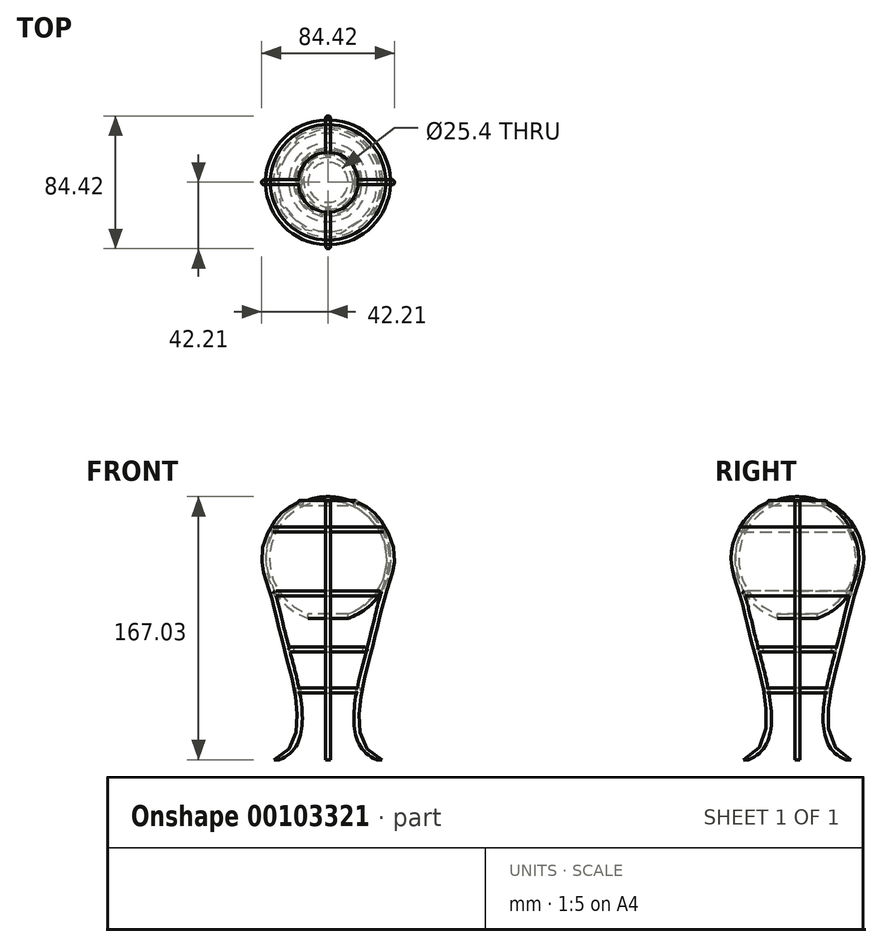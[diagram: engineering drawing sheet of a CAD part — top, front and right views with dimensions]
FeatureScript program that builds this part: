
annotation { "Feature Type Name" : "Feature", "Feature Type Description" : "" }
export const myFeature = defineFeature(function(context is Context, id is Id, definition is map)
    precondition{}
    {
        {
            var Q0;
            Q0=qCreatedBy(makeId("Front.planeOp"),FACE);
            var sketch = newSketch(context, id + "F0", { "sketchPlane" : qUnion([Q0])});
            skArc(sketch, "E0", {"start": v(0, 39.68) * mm, "mid": v(-39.68, 0) * mm, "end": v(0, -39.68) * mm});
            skLineSegment(sketch, "E1", {"start": v(0, -55.2) * mm, "end": v(0, 54.64) * mm});
            skSolve(sketch);
        }
        {
            var Q0;
            {var subQ0=sQuery(id+"F0.wireOp",EDGE,"E0");Q0=makeQuery(id+"F0.imprint","IMPRINT",FACE,{"disambiguationData":[TD([[makeQuery(id+"F0.imprint","IMPRINT",EDGE,{"derivedFrom":subQ0}),1.0]])]});}
            var Q1;
            Q1=sQuery(id+"F0.wireOp",EDGE,"E1");
            revolve(context, id + "F1", {"entities" : qUnion([Q0]), "axis" : qUnion([Q1]), "revolveType" : RevolveType.FULL});
        }
        {
            var Q0;
            Q0=qCreatedBy(makeId("Top.planeOp"),FACE);
            var sketch = newSketch(context, id + "F2", { "sketchPlane" : qUnion([Q0])});
            skCircle(sketch, "E2", {"center": v(0, 0) * mm, "radius": 12.7 * mm});
            skSolve(sketch);
        }
        {
            var Q0;
            Q0 = qSketchRegion(id + "F2", true);
            extrude(context, id + "F3", {"entities" : qUnion([Q0]), "operationType" : NewBodyOperationType.ADD, "oppositeDirection" : true, "depth" : 127 * mm});
        }
        {
            var Q0;
            Q0=makeQuery(id+"F3.opExtrude","SWEPT_FACE",FACE,{"disambiguationData":[OSD([sQuery(id+"F2.wireOp",EDGE,"E2")])]});
            var Q1;
            Q1=makeQuery(id+"F3.opExtrude","CAP_FACE",FACE,{"disambiguationData":[OSD([sQuery(id+"F2.wireOp",EDGE,"E2")])],"isStart":false});
            var Q2;
            Q2=makeQuery(id+"F1.opRevolve","SWEPT_BODY",BODY,{"disambiguationData":[OSD([sQuery(id+"F0.wireOp",EDGE,"E0"),sQuery(id+"F0.wireOp",EDGE,"E1")])]});
            shell(context, id + "F4", {"entities" : qUnion([Q0, Q1]), "parts" : qUnion([Q2]), "thickness" : 2.54 * mm});
        }
        {
            var Q0;
            Q0=qCreatedBy(makeId("Right.planeOp"),FACE);
            var sketch = newSketch(context, id + "F5", { "sketchPlane" : qUnion([Q0])});
            skCircle(sketch, "E3", {"center": v(-35.08, 18.94) * mm, "radius": 1.59 * mm});
            skCircle(sketch, "E4", {"center": v(-33.1, -21.72) * mm, "radius": 1.59 * mm});
            skCircle(sketch, "E5", {"center": v(-17.43, 35.83) * mm, "radius": 1.59 * mm});
            skSolve(sketch);
        }
        {
            var Q0;
            Q0=qCreatedBy(makeId("Front.planeOp"),FACE);
            var sketch = newSketch(context, id + "F6", { "sketchPlane" : qUnion([Q0])});
            skLineSegment(sketch, "E6", {"start": v(0, 56.6) * mm, "end": v(0, -57.7) * mm});
            skSolve(sketch);
        }
        {
            var Q0;
            Q0=qCreatedBy(makeId("Top.planeOp"),FACE);
            cPlane(context, id + "F7", {"entities" : qUnion([Q0]), "cplaneType" : CPlaneType.OFFSET, "offset" : 36.07 * mm, "width" : 152.4 * mm, "height" : 152.4 * mm});
        }
        {
            var Q0;
            Q0 = qSketchRegion(id + "F5", true);
            var Q1;
            Q1=sQuery(id+"F6.wireOp",EDGE,"E6");
            revolve(context, id + "F8", {"entities" : qUnion([Q0]), "axis" : qUnion([Q1]), "revolveType" : RevolveType.FULL});
        }
        {
            var Q0;
            Q0=qCreatedBy(id+"F7.planeOp",FACE);
            var sketch = newSketch(context, id + "F9", { "sketchPlane" : qUnion([Q0])});
            skCircle(sketch, "E7", {"center": v(-17.61, 0) * mm, "radius": 1.59 * mm});
            skSolve(sketch);
        }
        {
            var Q0;
            Q0=qCreatedBy(makeId("Front.planeOp"),FACE);
            var sketch = newSketch(context, id + "F10", { "sketchPlane" : qUnion([Q0])});
            skFitSpline(sketch, "E8", {"points": [v(-18.71, 36.13) * mm, v(-36.5, 19.47) * mm, v(-41.87, 0) * mm, v(-36.3, -22.17) * mm, v(-27.15, -58.35) * mm, v(-33.84, -127.35) * mm], "startDerivative": vector(-158.7, -63.01) * mm, "endDerivative": vector(-246.66, -91.65) * mm});
            skSolve(sketch);
        }
        {
            var Q0;
            Q0 = qSketchRegion(id + "F9", true);
            var Q1;
            Q1 = qConstructionFilter(qBodyType(qCreatedBy(id + "F10" ,EDGE), BodyType.WIRE), ConstructionObject.NO);
            sweep(context, id + "F11", {"profiles" : qUnion([Q0]), "path" : qUnion([Q1]), "keepProfileOrientation" : true});
        }
        {
            var Q0;
            Q0=makeQuery(id+"F11.opSweep","SWEPT_BODY",BODY,{"disambiguationData":[OSD([sQuery(id+"F9.wireOp",EDGE,"E7"),sQuery(id+"F10.wireOp",EDGE,"E8")])]});
            var Q1;
            Q1=sQuery(id+"F6.wireOp",EDGE,"E6");
            transform(context, id + "F12", {"entities" : qUnion([Q0]), "transformType" : TransformType.ROTATION, "transformAxis" : qUnion([Q1]), "angle" : 90 * degree, "makeCopy" : true});
        }
        {
            var Q0;
            Q0=makeQuery(id+"F11.opSweep","SWEPT_BODY",BODY,{"disambiguationData":[OSD([sQuery(id+"F9.wireOp",EDGE,"E7"),sQuery(id+"F10.wireOp",EDGE,"E8")])]});
            var Q1;
            Q1=sQuery(id+"F6.wireOp",EDGE,"E6");
            transform(context, id + "F13", {"entities" : qUnion([Q0]), "transformType" : TransformType.ROTATION, "transformAxis" : qUnion([Q1]), "angle" : 180 * degree, "makeCopy" : true});
        }
        {
            var Q0;
            Q0=makeQuery(id+"F11.opSweep","SWEPT_BODY",BODY,{"disambiguationData":[OSD([sQuery(id+"F9.wireOp",EDGE,"E7"),sQuery(id+"F10.wireOp",EDGE,"E8")])]});
            var Q1;
            Q1=sQuery(id+"F6.wireOp",EDGE,"E6");
            transform(context, id + "F14", {"entities" : qUnion([Q0]), "transformType" : TransformType.ROTATION, "transformAxis" : qUnion([Q1]), "angle" : 90 * degree, "oppositeDirection" : true, "makeCopy" : true});
        }
        {
            var Q0;
            Q0=qCreatedBy(makeId("Right.planeOp"),FACE);
            var sketch = newSketch(context, id + "F15", { "sketchPlane" : qUnion([Q0])});
            skCircle(sketch, "E9", {"center": v(-23.42, -57.4) * mm, "radius": 1.59 * mm});
            skCircle(sketch, "E10", {"center": v(-19.12, -83.22) * mm, "radius": 1.59 * mm});
            skSolve(sketch);
        }
        {
            var Q0;
            Q0=makeQuery(id+"F15.imprint","IMPRINT",FACE,{"disambiguationData":[TD([[makeQuery(id+"F15.imprint","IMPRINT",EDGE,{"derivedFrom":sQuery(id+"F15.wireOp",EDGE,"E9")}),1.0]])]});
            var Q1;
            Q1=makeQuery(id+"F15.imprint","IMPRINT",FACE,{"disambiguationData":[TD([[makeQuery(id+"F15.imprint","IMPRINT",EDGE,{"derivedFrom":sQuery(id+"F15.wireOp",EDGE,"E10")}),1.0]])]});
            var Q2;
            Q2=sQuery(id+"F6.wireOp",EDGE,"E6");
            revolve(context, id + "F16", {"entities" : qUnion([Q0, Q1]), "axis" : qUnion([Q2]), "revolveType" : RevolveType.FULL});
        }
    });
